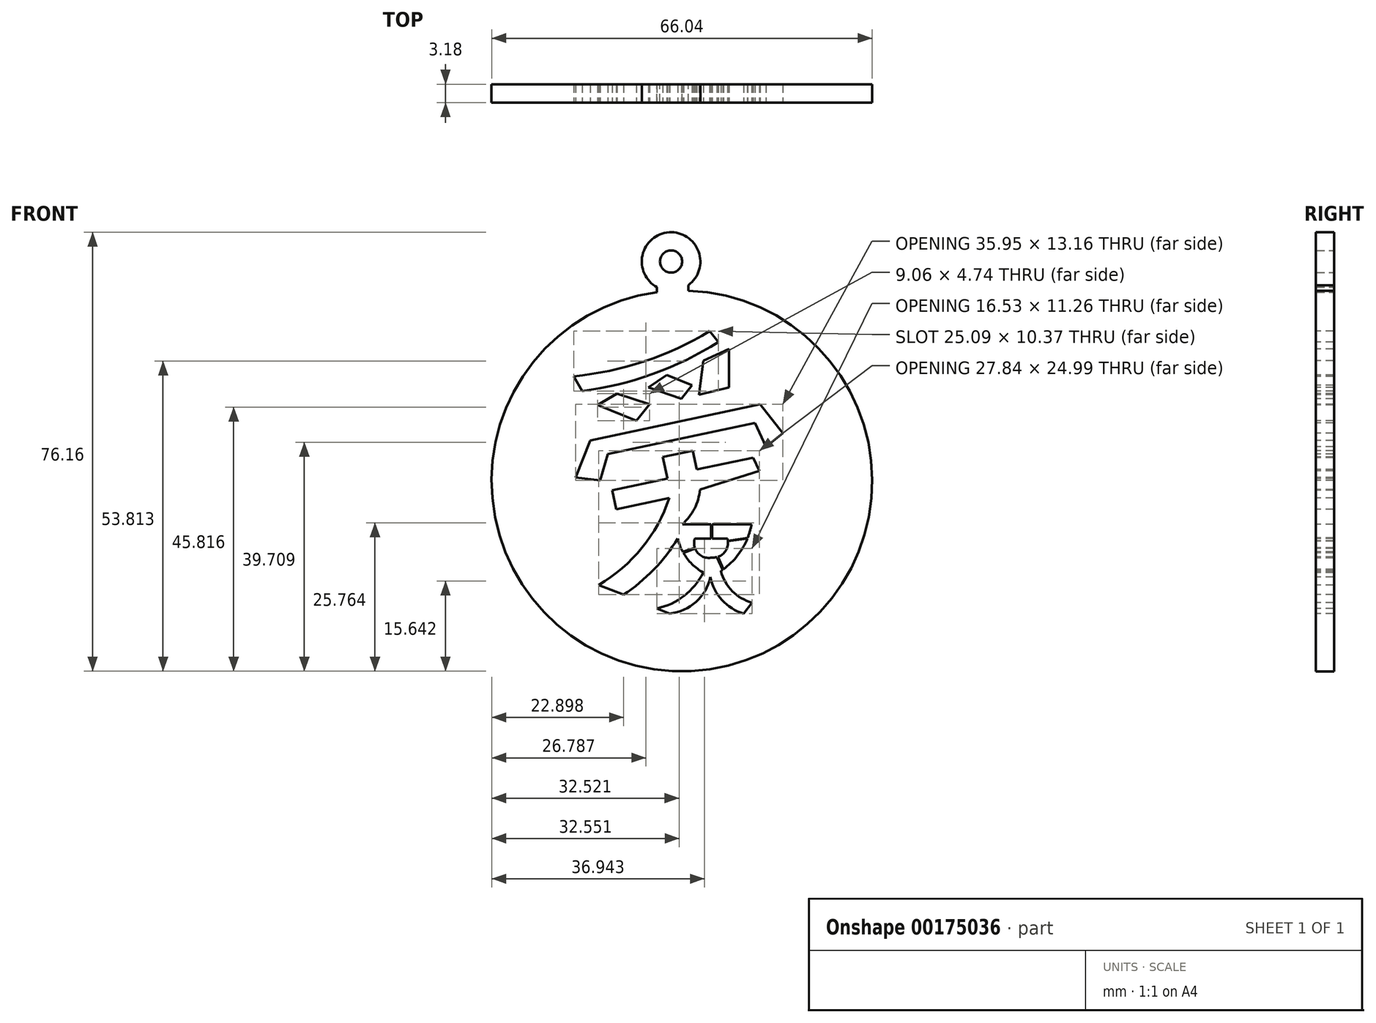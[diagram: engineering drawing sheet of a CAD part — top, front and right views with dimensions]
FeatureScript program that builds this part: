
annotation { "Feature Type Name" : "Feature", "Feature Type Description" : "" }
export const myFeature = defineFeature(function(context is Context, id is Id, definition is map)
    precondition{}
    {
        {
            var Q0;
            Q0=qCreatedBy(makeId("Front.planeOp"),FACE);
            var sketch = newSketch(context, id + "F0", { "sketchPlane" : qUnion([Q0])});
            skCircle(sketch, "E0", {"center": v(39.7, 37.68) * mm, "radius": 33.02 * mm});
            skCircle(sketch, "E1", {"center": v(37.81, 75.74) * mm, "radius": 1.92 * mm});
            skCircle(sketch, "E2", {"center": v(37.81, 75.74) * mm, "radius": 5.08 * mm});
            skLineSegment(sketch, "E3", {"start": v(40.82, 71.64) * mm, "end": v(40.82, 70.68) * mm});
            skLineSegment(sketch, "E4", {"start": v(35.37, 71.29) * mm, "end": v(35.37, 70.41) * mm});
            skSolve(sketch);
        }
        {
            var Q0;
            Q0 = qSketchRegion(id + "F0", true);
            extrude(context, id + "F1", {"entities" : qUnion([Q0]), "depth" : 3.17 * mm});
        }
        {
            var Q0;
            Q0=makeQuery(id+"F1.opExtrude","CAP_FACE",FACE,{"disambiguationData":[OSD([sQuery(id+"F0.wireOp",EDGE,"E0"),sQuery(id+"F0.wireOp",EDGE,"E1"),sQuery(id+"F0.wireOp",EDGE,"E2"),sQuery(id+"F0.wireOp",EDGE,"E3"),sQuery(id+"F0.wireOp",EDGE,"E4")])],"isStart":false});
            var sketch = newSketch(context, id + "F2", { "sketchPlane" : qUnion([Q0])});
            skArc(sketch, "E5", {"start": v(20.92, 55.82) * mm, "mid": v(33.15, 58.43) * mm, "end": v(44.52, 63.66) * mm});
            skLineSegment(sketch, "E6", {"start": v(20.92, 55.82) * mm, "end": v(22.4, 53.29) * mm});
            skLineSegment(sketch, "E7", {"start": v(44.52, 63.66) * mm, "end": v(46.01, 61.78) * mm});
            skArc(sketch, "E8", {"start": v(22.4, 53.29) * mm, "mid": v(34.67, 56.24) * mm, "end": v(46.01, 61.78) * mm});
            skLineSegment(sketch, "E9", {"start": v(25.05, 50.87) * mm, "end": v(31.8, 48.1) * mm});
            skLineSegment(sketch, "E10", {"start": v(31.8, 48.1) * mm, "end": v(34.1, 50.96) * mm});
            skLineSegment(sketch, "E11", {"start": v(34.1, 50.96) * mm, "end": v(28.44, 52.85) * mm});
            skLineSegment(sketch, "E12", {"start": v(28.44, 52.85) * mm, "end": v(25.05, 50.87) * mm});
            skLineSegment(sketch, "E13", {"start": v(33.9, 53.93) * mm, "end": v(39.58, 51.94) * mm});
            skLineSegment(sketch, "E14", {"start": v(39.58, 51.94) * mm, "end": v(41.47, 54.3) * mm});
            skLineSegment(sketch, "E15", {"start": v(41.47, 54.3) * mm, "end": v(37.04, 56.05) * mm});
            skLineSegment(sketch, "E16", {"start": v(37.04, 56.05) * mm, "end": v(33.9, 53.93) * mm});
            skLineSegment(sketch, "E17", {"start": v(43.4, 58.51) * mm, "end": v(42.68, 52.61) * mm});
            skLineSegment(sketch, "E18", {"start": v(42.68, 52.61) * mm, "end": v(47.85, 53.93) * mm});
            skLineSegment(sketch, "E19", {"start": v(47.85, 53.93) * mm, "end": v(47.85, 60.59) * mm});
            skLineSegment(sketch, "E20", {"start": v(47.85, 60.59) * mm, "end": v(43.4, 58.51) * mm});
            skLineSegment(sketch, "E21", {"start": v(23.77, 44.69) * mm, "end": v(21.26, 38.3) * mm});
            skLineSegment(sketch, "E22", {"start": v(21.26, 38.3) * mm, "end": v(25.5, 37.79) * mm});
            skLineSegment(sketch, "E23", {"start": v(25.5, 37.79) * mm, "end": v(26.83, 42.35) * mm});
            skLineSegment(sketch, "E24", {"start": v(26.83, 42.35) * mm, "end": v(52.35, 47.74) * mm});
            skLineSegment(sketch, "E25", {"start": v(52.35, 47.74) * mm, "end": v(54.27, 43.64) * mm});
            skLineSegment(sketch, "E26", {"start": v(54.27, 43.64) * mm, "end": v(57.2, 45.95) * mm});
            skLineSegment(sketch, "E27", {"start": v(57.2, 45.95) * mm, "end": v(53.28, 50.95) * mm});
            skLineSegment(sketch, "E28", {"start": v(53.28, 50.95) * mm, "end": v(23.77, 44.69) * mm});
            skLineSegment(sketch, "E29", {"start": v(36.38, 41.82) * mm, "end": v(41.57, 42.92) * mm});
            skLineSegment(sketch, "E30", {"start": v(41.57, 42.92) * mm, "end": v(42.26, 39.65) * mm});
            skLineSegment(sketch, "E31", {"start": v(42.26, 39.65) * mm, "end": v(52.06, 41.72) * mm});
            skLineSegment(sketch, "E32", {"start": v(52.06, 41.72) * mm, "end": v(53.12, 39.44) * mm});
            skLineSegment(sketch, "E33", {"start": v(53.12, 39.44) * mm, "end": v(42.83, 36.16) * mm});
            skArc(sketch, "E34", {"start": v(39.78, 30.16) * mm, "mid": v(41.87, 32.88) * mm, "end": v(42.83, 36.16) * mm});
            skLineSegment(sketch, "E35", {"start": v(39.78, 30.16) * mm, "end": v(51.78, 30.16) * mm});
            skArc(sketch, "E36", {"start": v(46.45, 22.03) * mm, "mid": v(49.93, 25.56) * mm, "end": v(51.78, 30.16) * mm});
            skLineSegment(sketch, "E37", {"start": v(36.38, 41.82) * mm, "end": v(37.17, 38.07) * mm});
            skLineSegment(sketch, "E38", {"start": v(37.17, 38.07) * mm, "end": v(27.6, 36.05) * mm});
            skLineSegment(sketch, "E39", {"start": v(27.6, 36.05) * mm, "end": v(28.3, 32.78) * mm});
            skLineSegment(sketch, "E40", {"start": v(28.3, 32.78) * mm, "end": v(37.5, 34.73) * mm});
            skArc(sketch, "E41", {"start": v(25.28, 19.63) * mm, "mid": v(32.76, 26.07) * mm, "end": v(37.5, 34.73) * mm});
            skLineSegment(sketch, "E42", {"start": v(25.28, 19.63) * mm, "end": v(29.58, 17.93) * mm});
            skArc(sketch, "E43", {"start": v(29.58, 17.93) * mm, "mid": v(34.81, 22.3) * mm, "end": v(38.97, 27.7) * mm});
            skArc(sketch, "E44", {"start": v(38.97, 27.7) * mm, "mid": v(40.56, 24.27) * mm, "end": v(43.4, 21.78) * mm});
            skArc(sketch, "E45", {"start": v(41.93, 27.7) * mm, "mid": v(42.47, 25.17) * mm, "end": v(44.93, 24.4) * mm});
            skLineSegment(sketch, "E46", {"start": v(41.93, 27.7) * mm, "end": v(47.59, 27.7) * mm});
            skArc(sketch, "E47", {"start": v(44.93, 24.4) * mm, "mid": v(47.13, 25.34) * mm, "end": v(47.59, 27.7) * mm});
            skArc(sketch, "E48", {"start": v(35.36, 15.55) * mm, "mid": v(40.09, 17.75) * mm, "end": v(43.4, 21.78) * mm});
            skLineSegment(sketch, "E49", {"start": v(35.36, 15.55) * mm, "end": v(37.58, 14.67) * mm});
            skArc(sketch, "E50", {"start": v(37.58, 14.67) * mm, "mid": v(42.14, 16.68) * mm, "end": v(44.64, 20.98) * mm});
            skArc(sketch, "E51", {"start": v(44.64, 20.98) * mm, "mid": v(46.65, 17.02) * mm, "end": v(50.42, 14.67) * mm});
            skLineSegment(sketch, "E52", {"start": v(50.42, 14.67) * mm, "end": v(51.89, 16.57) * mm});
            skArc(sketch, "E53", {"start": v(46.45, 22.03) * mm, "mid": v(48.43, 18.56) * mm, "end": v(51.89, 16.57) * mm});
            skLineSegment(sketch, "E54", {"start": v(46.75, 22.24) * mm, "end": v(45.77, 24.47) * mm});
            skLineSegment(sketch, "E55", {"start": v(45.97, 24.53) * mm, "end": v(46.9, 22.35) * mm});
            skLineSegment(sketch, "E56", {"start": v(41.93, 26.1) * mm, "end": v(39.83, 25.42) * mm});
            skLineSegment(sketch, "E57", {"start": v(39.96, 25.2) * mm, "end": v(41.99, 25.93) * mm});
            skLineSegment(sketch, "E58", {"start": v(47.67, 27.32) * mm, "end": v(51.1, 27.8) * mm});
            skLineSegment(sketch, "E59", {"start": v(47.68, 27.22) * mm, "end": v(51.08, 27.7) * mm});
            skLineSegment(sketch, "E60", {"start": v(44.76, 27.7) * mm, "end": v(44.76, 30.16) * mm});
            skLineSegment(sketch, "E61", {"start": v(44.95, 27.7) * mm, "end": v(44.95, 30.16) * mm});
            skSolve(sketch);
        }
        {
            var Q0;
            Q0=makeQuery(id+"F2.imprint","IMPRINT",FACE,{"disambiguationData":[TD([[makeQuery(id+"F2.imprint","IMPRINT",EDGE,{"derivedFrom":sQuery(id+"F2.wireOp",EDGE,"E5")}),-1.0]])]});
            var Q1;
            Q1=makeQuery(id+"F2.imprint","IMPRINT",FACE,{"disambiguationData":[TD([[makeQuery(id+"F2.imprint","IMPRINT",EDGE,{"derivedFrom":sQuery(id+"F2.wireOp",EDGE,"E9")}),1.0]])]});
            var Q2;
            Q2=makeQuery(id+"F2.imprint","IMPRINT",FACE,{"disambiguationData":[TD([[makeQuery(id+"F2.imprint","IMPRINT",EDGE,{"derivedFrom":sQuery(id+"F2.wireOp",EDGE,"E13")}),1.0]])]});
            var Q3;
            Q3=makeQuery(id+"F2.imprint","IMPRINT",FACE,{"disambiguationData":[TD([[makeQuery(id+"F2.imprint","IMPRINT",EDGE,{"derivedFrom":sQuery(id+"F2.wireOp",EDGE,"E17")}),1.0]])]});
            var Q4;
            Q4=makeQuery(id+"F2.imprint","IMPRINT",FACE,{"disambiguationData":[TD([[makeQuery(id+"F2.imprint","IMPRINT",EDGE,{"derivedFrom":sQuery(id+"F2.wireOp",EDGE,"E21")}),1.0]])]});
            var Q5;
            {var subQ1=sQuery(id+"F2.wireOp",EDGE,"E48");Q5=makeQuery(id+"F2.imprint","IMPRINT",FACE,{"disambiguationData":[TD([[makeQuery(id+"F2.imprint","IMPRINT",EDGE,{"derivedFrom":subQ1}),-1.0]])]});}
            var Q6;
            Q6=makeQuery(id+"F2.imprint","IMPRINT",FACE,{"disambiguationData":[TD([[makeQuery(id+"F2.imprint","IMPRINT",EDGE,{"derivedFrom":sQuery(id+"F2.wireOp",EDGE,"E29")}),-1.0]])]});
            var Q7;
            {var subQ7=sQuery(id+"F2.wireOp",EDGE,"E58");Q7=makeQuery(id+"F2.imprint","IMPRINT",FACE,{"disambiguationData":[TD([[makeQuery(id+"F2.imprint","IMPRINT",EDGE,{"derivedFrom":subQ7}),1.0]])]});}
            var Q8;
            {var subQ0=sQuery(id+"F2.wireOp",EDGE,"E55");Q8=makeQuery(id+"F2.imprint","IMPRINT",FACE,{"disambiguationData":[TD([[makeQuery(id+"F2.imprint","IMPRINT",EDGE,{"derivedFrom":subQ0}),1.0]])]});}
            extrude(context, id + "F3", {"entities" : qUnion([Q0, Q1, Q2, Q3, Q4, Q5, Q6, Q7, Q8]), "operationType" : NewBodyOperationType.REMOVE, "oppositeDirection" : true, "depth" : 3.17 * mm});
        }
    });
